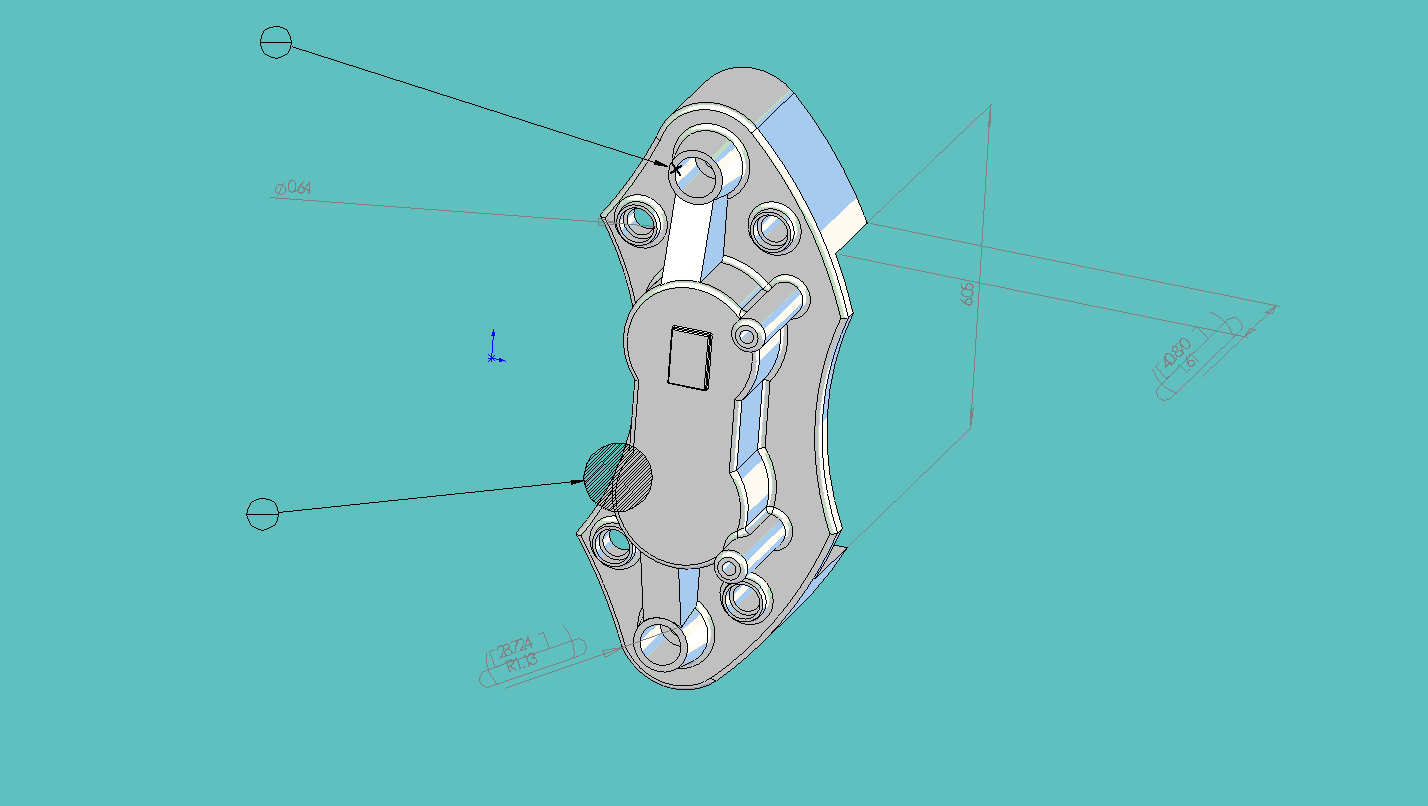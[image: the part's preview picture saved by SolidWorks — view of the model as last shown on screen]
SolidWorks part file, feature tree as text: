
SOLIDWORKS PART (.sldprt)
format: sldprt  version: not decoded by parser v0  size: 2,103,296 bytes
history: native  units: mm
features: sketch x25, cut_extrude x14, fillet x9, extrude x7, mirror x4, plane x3, material x1, chamfer x1, delete_body x1 + 1 further entry (+14 scaffold rows collapsed)
feature tree (80):
  scaffold x14  (default folders/planes/origin — collapsed)
  material  "Material <not specified>"
  "DetailItem2"  RD1=40.870077mm RD2=16.253517mm RD3=28.723789mm RD4=153.604076mm
  sketch  "Sketch1"  dims[D1=63.5mm]
  extrude  "Extrude1"  Depth=31.75mm
  sketch  "Sketch5"  dims[D1=~43.962388mm]
  extrude  "Extrude2"  Depth=50.8mm
  sketch  "Sketch3"  dims[D1=50.0mm]
  cut_extrude  "Cut-Extrude1"  Depth=25.4mm
  sketch  "Sketch7"  dims[c1.D1=12.7mm c1.D2=12.7mm c2.D1=~13.906952mm c2.D2=25.0mm c2.D3=25.0mm c3.D1=~12.799272mm c3.D3=152.4mm]
  fillet  "Fillet1"  Radius=2.54mm
  fillet  "Fillet2"  Radius=2.54mm
  fillet  "Fillet3"  Radius=2.54mm
  sketch  "Sketch10"
  cut_extrude  "Cut-Extrude3"  [1 undecoded]
  plane  "Plane1"  Offset=10.16mm
  plane  "Plane2"  Offset=8.636mm
  sketch  "Sketch13"  dims[D1=273.05mm D2=137.16mm]
  cut_extrude  "Cut-Extrude4"  [1 undecoded]
  sketch  "Sketch14"
  cut_extrude  "Cut-Extrude5"  [1 undecoded]
  sketch  "Sketch15"
  extrude  "Extrude3"  Depth=53.18mm
  fillet  "Fillet4"  Radius=2.54mm
  sketch  "Sketch16"  dims[D1=~1.636236mm]
  cut_extrude  "Cut-Extrude6"  Depth=27.94mm
  fillet  "Fillet5"  Radius=2.54mm
  sketch  "Sketch17"
  extrude  "Extrude4"  Depth=2.54mm
  fillet  "Fillet6"  Radius=0.508mm
  chamfer  "Chamfer1"  Distance=1.27mm Angle=45deg
  sketch  "Sketch20"  dims[c1.D1=31.75mm c1.D2=25.4mm c2.D1=~20.003376mm]
  extrude  "Extrude5"  Depth=20.32mm
  cut_extrude  "Cut-Extrude8"  [1 undecoded]
  sketch  "Sketch21"  dims[D1=~4.108238mm]
  cut_extrude  "Cut-Extrude10"  Depth=25.4mm
  fillet  "Fillet7"  Radius=2.54mm
  sketch  "Sketch22"  dims[D1=10.16mm]
  cut_extrude  "Cut-Extrude11"  [1 undecoded]
  sketch  "Sketch24"
  cut_extrude  "Cut-Extrude12"  Depth=22.86mm
  sketch  "Sketch25"  dims[D1=20.574mm]
  extrude  "Extrude6"  Depth=5.08mm
  fillet  "Fillet8"  Radius=2.54mm
  sketch  "Sketch27"  dims[D1=~16.253517mm]
  cut_extrude  "Cut-Extrude15"  Depth=5.08mm
  mirror  "Mirror1"
  sketch  "Sketch29"  dims[D1=7.62mm]
  extrude  "Extrude7"  [1 undecoded]
  sketch  "Sketch30"
  sketch  "Sketch31"  dims[D1=5.08mm]
  cut_extrude  "Cut-Extrude18"  Depth=16.392582mm
  sketch  "Sketch32"  dims[D1=8.89mm]
  cut_extrude  "Cut-Extrude19"  Depth=16.392582mm
  cut_extrude  "Cut-Extrude20"  Depth=43.688mm
  sketch  "Sketch33"
  cut_extrude  "Cut-Extrude21"  Depth=59.69mm
  fillet  "Fillet11"  Radius=2.54mm
  plane  "Plane3"  Offset=94.488mm
  sketch  "Sketch34"  dims[D1=17.62mm]
  sketch  "Sketch36"
  mirror  "Rib3"
  sketch  "Sketch38"
  mirror  "Rib4"
  sketch  "Sketch40"
  mirror  "Rib5"
  delete_body  "Body-Delete1"
decode coverage: 40 of 61 modeling features carry decoded parameters; 1 rows unclassified (native names shown)
note: ~ marks probable driven/reference dimensions
note: 6 parameter values undecoded
summary: no parameter record found for 6 features
note: suppression state not decoded; provenance and decode notes live in map.json
